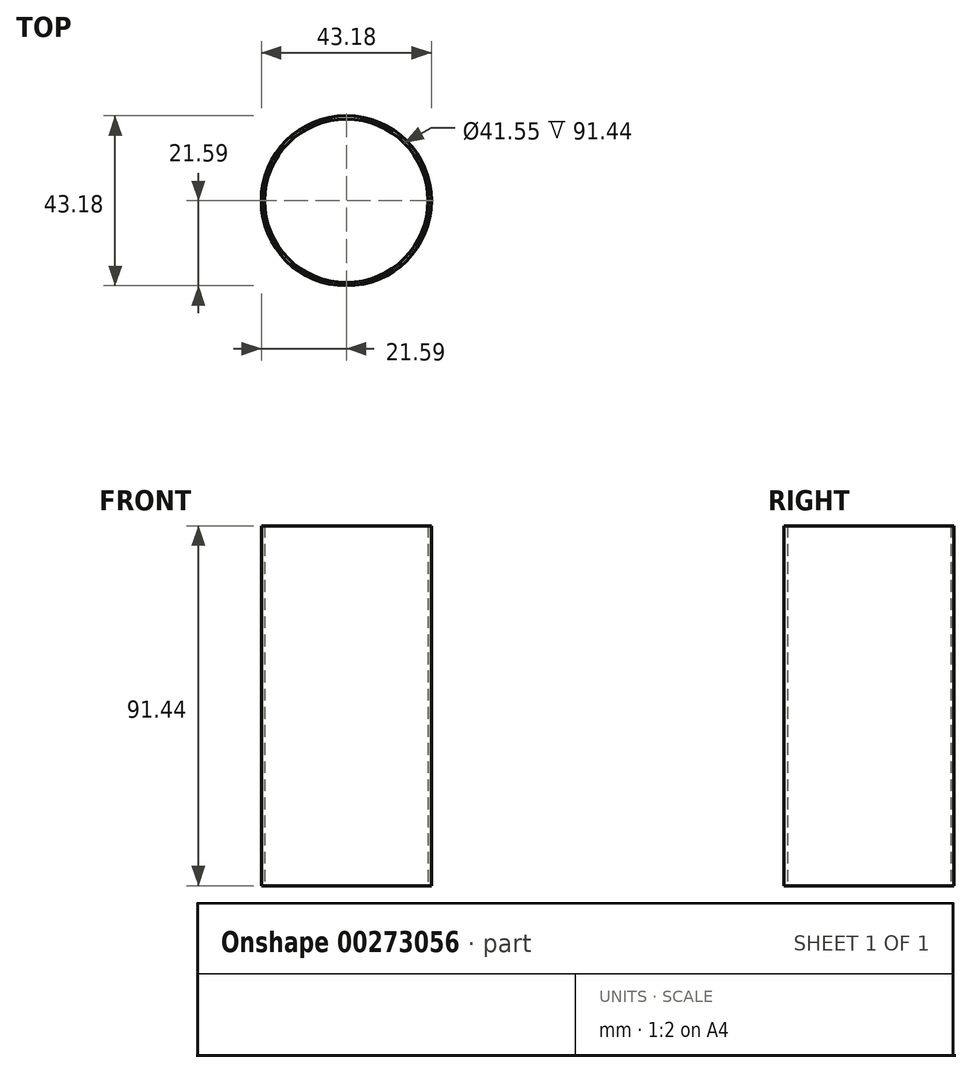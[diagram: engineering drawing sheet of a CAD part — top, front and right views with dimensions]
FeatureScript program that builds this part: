
annotation { "Feature Type Name" : "Feature", "Feature Type Description" : "" }
export const myFeature = defineFeature(function(context is Context, id is Id, definition is map)
    precondition{}
    {
        {
            var Q0;
            Q0=qCreatedBy(makeId("Top.planeOp"),FACE);
            var sketch = newSketch(context, id + "F0", { "sketchPlane" : qUnion([Q0])});
            skCircle(sketch, "E0", {"center": v(0, 0) * mm, "radius": 20.78 * mm});
            skCircle(sketch, "E1", {"center": v(0, 0) * mm, "radius": 21.59 * mm});
            skSolve(sketch);
        }
        {
            var Q0;
            Q0=qSketchRegion(id+"F0",true);
            extrude(context, id + "F1", {"entities" : qUnion([Q0]), "depth" : 91.44 * mm});
        }
    });
